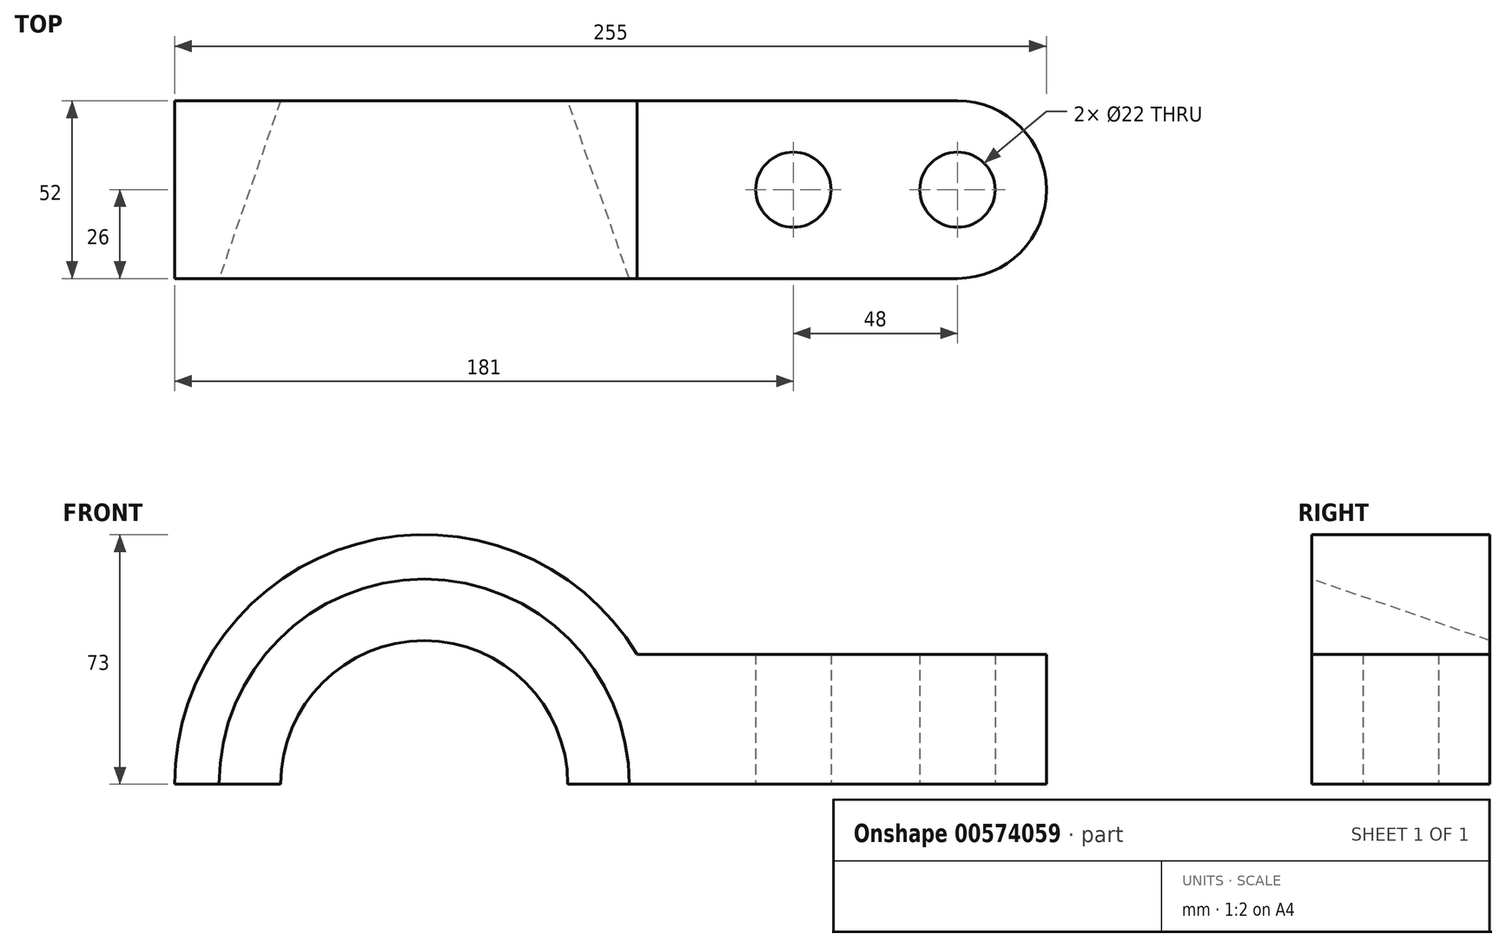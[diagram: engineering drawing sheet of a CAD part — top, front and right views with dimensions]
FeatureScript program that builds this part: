
annotation { "Feature Type Name" : "Feature", "Feature Type Description" : "" }
export const myFeature = defineFeature(function(context is Context, id is Id, definition is map)
    precondition{}
    {
        {
            var Q0;
            Q0=qCreatedBy(makeId("Front.planeOp"),FACE);
            var sketch = newSketch(context, id + "F0", { "sketchPlane" : qUnion([Q0])});
            skArc(sketch, "E0", {"start": v(62.33, 38) * mm, "mid": v(-19.73, 70.28) * mm, "end": v(-73, 0) * mm});
            skLineSegment(sketch, "E1.bottom", {"start": v(62.33, 38) * mm, "end": v(182, 38) * mm});
            skLineSegment(sketch, "E1.right", {"start": v(182, 38) * mm, "end": v(182, 0) * mm});
            skLineSegment(sketch, "E2", {"start": v(-73, 0) * mm, "end": v(182, 0) * mm});
            skSolve(sketch);
        }
        {
            var Q0;
            Q0 = qSketchRegion(id + "F0", true);
            extrude(context, id + "F1", {"entities" : qUnion([Q0]), "depth" : 52 * mm, "offsetDistance" : 25 * mm});
        }
        {
            var Q0;
            Q0=makeQuery(id+"F1.opExtrude","SWEPT_FACE",FACE,{"disambiguationData":[OSD([sQuery(id+"F0.wireOp",EDGE,"E2")])]});
            var sketch = newSketch(context, id + "F2", { "sketchPlane" : qUnion([Q0])});
            skLineSegment(sketch, "E3", {"start": v(-60, 52) * mm, "end": v(-42, 0) * mm});
            skLineSegment(sketch, "E4", {"start": v(-42, 0) * mm, "end": v(0, 0) * mm});
            skLineSegment(sketch, "E5", {"start": v(0, 0) * mm, "end": v(0, 52) * mm});
            skLineSegment(sketch, "E6", {"start": v(0, 52) * mm, "end": v(-60, 52) * mm});
            skSolve(sketch);
        }
        {
            var Q0;
            Q0 = qSketchRegion(id + "F2", true);
            var Q1;
            Q1=sQuery(id+"F2.wireOp",EDGE,"E5");
            revolve(context, id + "F3", {"operationType" : NewBodyOperationType.REMOVE, "entities" : qUnion([Q0]), "axis" : qUnion([Q1]), "revolveType" : RevolveType.FULL, "oppositeDirection" : true});
        }
        {
            var Q0;
            {var subQ0=sQuery(id+"F0.wireOp",EDGE,"E2");var subQ1=sQuery(id+"F0.wireOp",EDGE,"E1.right");Q0=makeQuery(id+"F3.boolean.opBoolean","SPLIT",FACE,{"disambiguationData":[TD([makeQuery(id+"F1.opExtrude","SWEPT_FACE",FACE,{"disambiguationData":[OSD([subQ1])]})])],"derivedFrom":makeQuery(id+"F1.opExtrude","SWEPT_FACE",FACE,{"disambiguationData":[OSD([subQ0])]})});}
            var sketch = newSketch(context, id + "F4", { "sketchPlane" : qUnion([Q0])});
            skCircle(sketch, "E7", {"center": v(108, 26) * mm, "radius": 11 * mm});
            skCircle(sketch, "E8", {"center": v(156, 26) * mm, "radius": 11 * mm});
            skSolve(sketch);
        }
        {
            var Q0;
            Q0 = qSketchRegion(id + "F4", true);
            extrude(context, id + "F5", {"entities" : qUnion([Q0]), "operationType" : NewBodyOperationType.REMOVE, "oppositeDirection" : true, "depth" : 77 * mm, "offsetDistance" : 25 * mm});
        }
        {
            var Q0;
            Q0=makeQuery(id+"F1.opExtrude","CAP_EDGE",EDGE,{"disambiguationData":[OSD([sQuery(id+"F0.wireOp",EDGE,"E1.right")])],"isStart":false});
            var Q1;
            Q1=makeQuery(id+"F1.opExtrude","CAP_EDGE",EDGE,{"disambiguationData":[OSD([sQuery(id+"F0.wireOp",EDGE,"E1.right")])],"isStart":true});
            fillet(context, id + "F6", {"entities" : qUnion([Q0, Q1]), "radius" : 26 * mm, "tangentPropagation" : true, "allowEdgeOverflow" : false});
        }
    });
